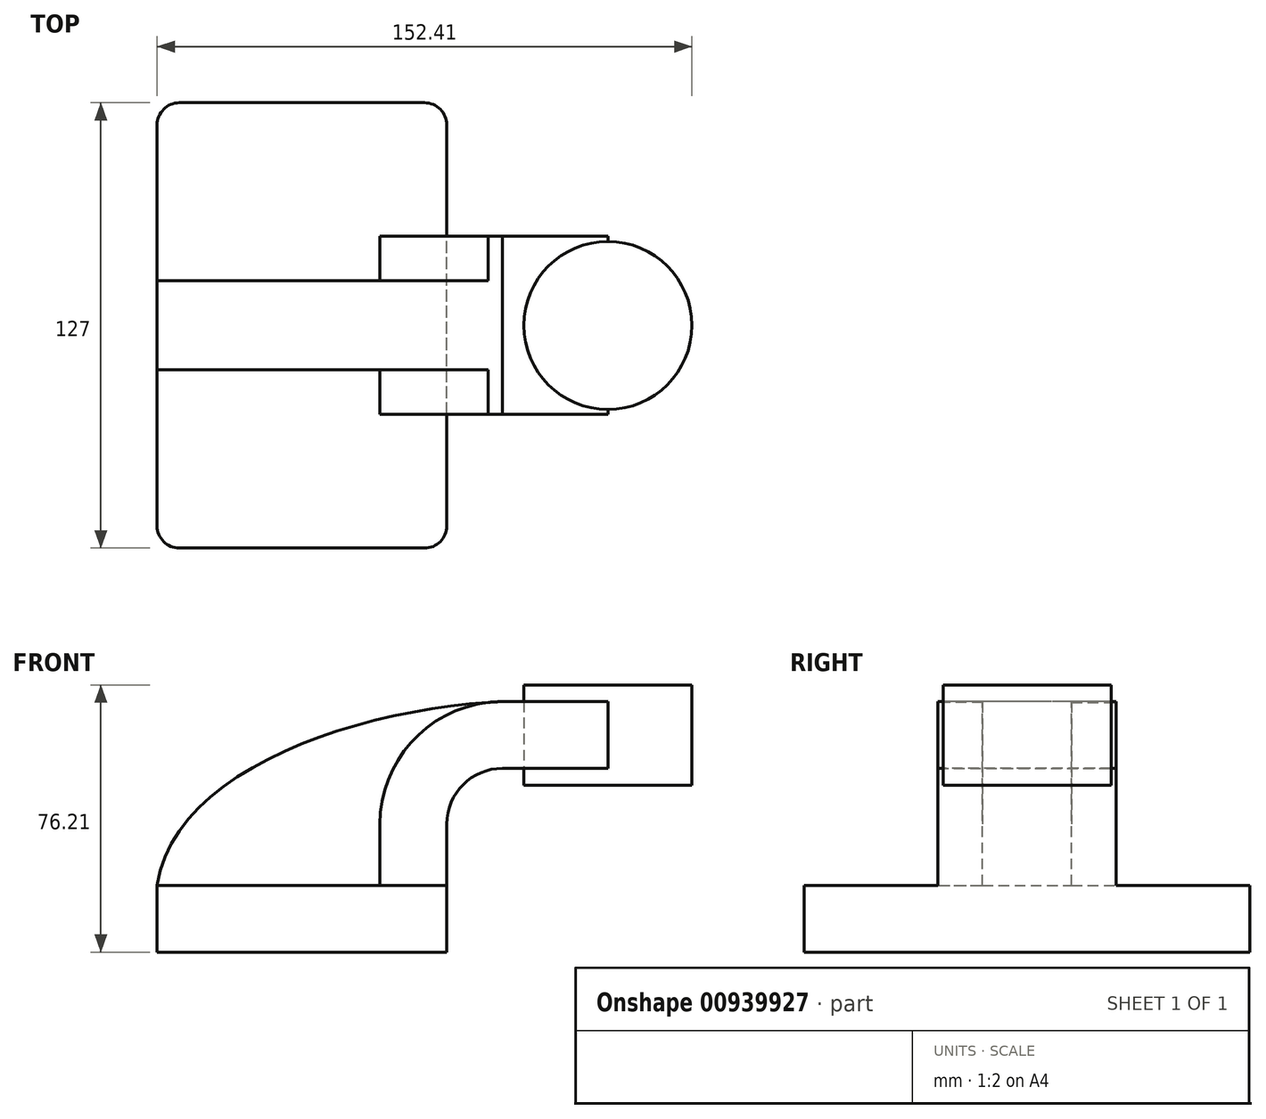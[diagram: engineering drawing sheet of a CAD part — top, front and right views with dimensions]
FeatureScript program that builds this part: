
annotation { "Feature Type Name" : "Feature", "Feature Type Description" : "" }
export const myFeature = defineFeature(function(context is Context, id is Id, definition is map)
    precondition{}
    {
        {
            var Q0;
            Q0=qCreatedBy(makeId("Front.planeOp"),FACE);
            var sketch = newSketch(context, id + "F0", { "sketchPlane" : qUnion([Q0])});
            skLineSegment(sketch, "E0.bottom", {"start": v(-41.28, 9.52) * mm, "end": v(41.28, 9.53) * mm});
            skLineSegment(sketch, "E0.top", {"start": v(-41.28, -9.53) * mm, "end": v(41.28, -9.53) * mm});
            skLineSegment(sketch, "E0.left", {"start": v(-41.28, 9.52) * mm, "end": v(-41.27, -9.53) * mm});
            skLineSegment(sketch, "E0.right", {"start": v(41.28, 9.53) * mm, "end": v(41.28, -9.52) * mm});
            skPoint(sketch, "E0.middle", {"position": v(0, 0) * mm});
            skLineSegment(sketch, "E1", {"start": v(41.27, 9.53) * mm, "end": v(41.27, 27) * mm});
            skLineSegment(sketch, "E2.bottom", {"start": v(60.32, 66.67) * mm, "end": v(111.12, 66.67) * mm});
            skLineSegment(sketch, "E2.top", {"start": v(60.32, 38.1) * mm, "end": v(111.12, 38.1) * mm});
            skLineSegment(sketch, "E2.left", {"start": v(60.32, 66.67) * mm, "end": v(60.32, 38.1) * mm});
            skLineSegment(sketch, "E2.right", {"start": v(111.12, 66.68) * mm, "end": v(111.12, 38.1) * mm});
            skPoint(sketch, "E2.middle", {"position": v(85.72, 52.39) * mm});
            skArc(sketch, "E3", {"start": v(41.27, 27) * mm, "mid": v(45.92, 38.23) * mm, "end": v(57.15, 42.88) * mm});
            skLineSegment(sketch, "E4", {"start": v(57.15, 42.88) * mm, "end": v(87.17, 42.88) * mm});
            skLineSegment(sketch, "E5.0", {"start": v(57.15, 61.93) * mm, "end": v(87.17, 61.93) * mm});
            skArc(sketch, "E5.1", {"start": v(22.22, 27) * mm, "mid": v(32.45, 51.7) * mm, "end": v(57.15, 61.93) * mm});
            skLineSegment(sketch, "E5.2", {"start": v(22.22, 9.53) * mm, "end": v(22.22, 27) * mm});
            skFitSpline(sketch, "E6", {"points": [v(-41.28, 9.52) * mm, v(57.15, 61.93) * mm], "startDerivative": vector(15, 99.92) * mm, "endDerivative": vector(122.6, 5.75) * mm});
            skLineSegment(sketch, "E7", {"start": v(87.17, 38.1) * mm, "end": v(87.17, 66.67) * mm});
            skSolve(sketch);
        }
        {
            var Q0;
            Q0=makeQuery(id+"F0.imprint","IMPRINT",FACE,{"disambiguationData":[TD([[makeQuery(id+"F0.imprint","IMPRINT",EDGE,{"derivedFrom":sQuery(id+"F0.wireOp",EDGE,"E0.top")}),1.0]])]});
            extrude(context, id + "F1", {"entities" : qUnion([Q0]), "depth" : 127 * mm, "offsetDistance" : 25.4 * mm, "symmetric" : true});
        }
        {
            var Q0;
            {var subQ1=sQuery(id+"F0.wireOp",EDGE,"E1");Q0=makeQuery(id+"F0.imprint","IMPRINT",FACE,{"disambiguationData":[TD([[makeQuery(id+"F0.imprint","IMPRINT",EDGE,{"derivedFrom":subQ1}),1.0]])]});}
            var Q1;
            {var subQ5=sQuery(id+"F0.wireOp",EDGE,"Fsr22RHa-ngiQ-wecc-DlJi-ZKups7MQOKca");Q1=makeQuery(id+"F0.imprint","IMPRINT",FACE,{"disambiguationData":[TD([[makeQuery(id+"F0.imprint","IMPRINT",EDGE,{"derivedFrom":subQ5}),1.0]])]});}
            var Q2;
            {var subQ0=sQuery(id+"F0.wireOp",EDGE,"E5.0");var subQ1=sQuery(id+"F0.wireOp",EDGE,"E2.left");var subQ2=makeQuery(id+"F0.imprint","INTERSECT",VERTEX,{"derivedFrom":[subQ1,subQ0]});Q2=makeQuery(id+"F0.imprint","IMPRINT",FACE,{"disambiguationData":[TD([[makeQuery(id+"F0.imprint","IMPRINT",EDGE,{"disambiguationData":[TD([[subQ2,-1.0]])],"derivedFrom":subQ1}),1.0]])]});}
            extrude(context, id + "F2", {"entities" : qUnion([Q0, Q1, Q2]), "operationType" : NewBodyOperationType.ADD, "depth" : 50.8 * mm, "offsetDistance" : 25.4 * mm, "symmetric" : true});
        }
        {
            var Q0;
            {var subQ3=sQuery(id+"F0.wireOp",EDGE,"E5.2");Q0=makeQuery(id+"F0.imprint","IMPRINT",FACE,{"disambiguationData":[TD([[makeQuery(id+"F0.imprint","IMPRINT",EDGE,{"derivedFrom":subQ3}),1.0]])]});}
            extrude(context, id + "F3", {"entities" : qUnion([Q0]), "operationType" : NewBodyOperationType.ADD, "depth" : 25.4 * mm, "offsetDistance" : 25.4 * mm, "symmetric" : true});
        }
        {
            var Q0;
            {var subQ0=sQuery(id+"F0.wireOp",EDGE,"E2.right");Q0=makeQuery(id+"F0.imprint","IMPRINT",FACE,{"disambiguationData":[TD([[makeQuery(id+"F0.imprint","IMPRINT",EDGE,{"derivedFrom":subQ0}),-1.0]])]});}
            var Q1;
            Q1=sQuery(id+"F0.wireOp",EDGE,"E7");
            revolve(context, id + "F4", {"surfaceOperationType" : NewSurfaceOperationType.NEW, "entities" : qUnion([Q0]), "axis" : qUnion([Q1]), "revolveType" : RevolveType.FULL});
        }
        {
            var Q0;
            Q0=makeQuery(id+"F1.opExtrude","CAP_EDGE",EDGE,{"disambiguationData":[OSD([sQuery(id+"F0.wireOp",EDGE,"E0.left")])],"isStart":false});
            var Q1;
            Q1=makeQuery(id+"F1.opExtrude","CAP_EDGE",EDGE,{"disambiguationData":[OSD([sQuery(id+"F0.wireOp",EDGE,"E0.right")])],"isStart":false});
            var Q2;
            Q2=makeQuery(id+"F1.opExtrude","CAP_EDGE",EDGE,{"disambiguationData":[OSD([sQuery(id+"F0.wireOp",EDGE,"E0.right")])],"isStart":true});
            var Q3;
            Q3=makeQuery(id+"F1.opExtrude","CAP_EDGE",EDGE,{"disambiguationData":[OSD([sQuery(id+"F0.wireOp",EDGE,"E0.left")])],"isStart":true});
            fillet(context, id + "F5", {"entities" : qUnion([Q0, Q1, Q2, Q3]), "radius" : 6.35 * mm, "tangentPropagation" : true, "allowEdgeOverflow" : false});
        }
    });
